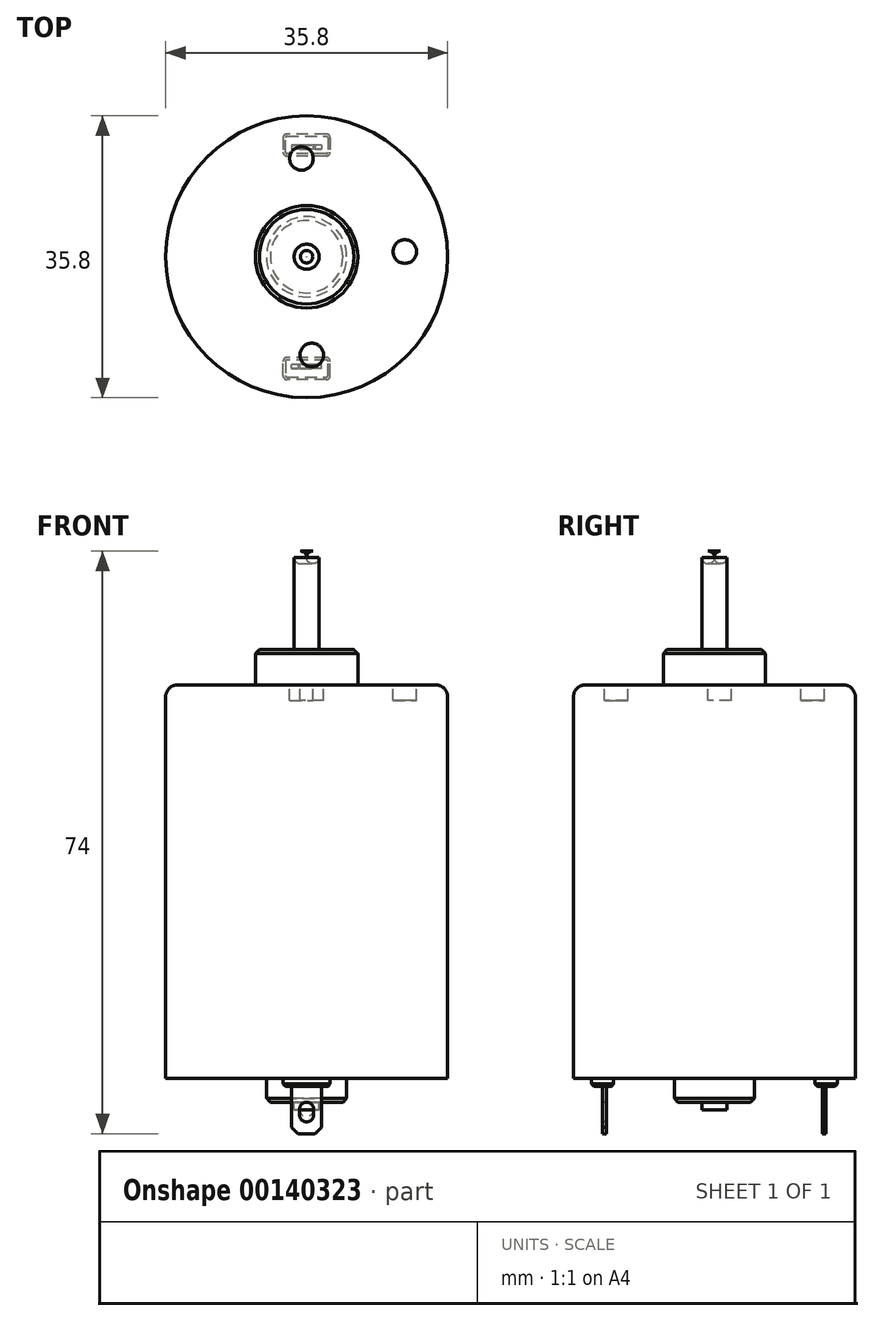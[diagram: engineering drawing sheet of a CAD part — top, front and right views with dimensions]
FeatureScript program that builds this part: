
annotation { "Feature Type Name" : "Feature", "Feature Type Description" : "" }
export const myFeature = defineFeature(function(context is Context, id is Id, definition is map)
    precondition{}
    {
        {
            var Q0;
            Q0=qCreatedBy(makeId("Top.planeOp"),FACE);
            var sketch = newSketch(context, id + "F0", { "sketchPlane" : qUnion([Q0])});
            skCircle(sketch, "E0", {"center": v(0, 0) * mm, "radius": 17.9 * mm});
            skSolve(sketch);
        }
        {
            var Q0;
            Q0=makeQuery(id+"F0.imprint","IMPRINT",FACE,{"disambiguationData":[TD([[makeQuery(id+"F0.imprint","IMPRINT",EDGE,{"derivedFrom":sQuery(id+"F0.wireOp",EDGE,"E0")}),1.0]])]});
            extrude(context, id + "F1", {"entities" : qUnion([Q0]), "depth" : 50 * mm});
        }
        {
            var Q0;
            Q0=makeQuery(id+"F1.opExtrude","CAP_FACE",FACE,{"disambiguationData":[OSD([sQuery(id+"F0.wireOp",EDGE,"E0")])],"isStart":true});
            var sketch = newSketch(context, id + "F2", { "sketchPlane" : qUnion([Q0])});
            skCircle(sketch, "E1", {"center": v(0, 0) * mm, "radius": 5.1 * mm});
            skSolve(sketch);
        }
        {
            var Q0;
            Q0=makeQuery(id+"F2.imprint","IMPRINT",FACE,{"disambiguationData":[TD([[makeQuery(id+"F2.imprint","IMPRINT",EDGE,{"derivedFrom":sQuery(id+"F2.wireOp",EDGE,"E1")}),1.0]])]});
            extrude(context, id + "F3", {"entities" : qUnion([Q0]), "operationType" : NewBodyOperationType.ADD, "depth" : 3 * mm});
        }
        {
            var Q0;
            Q0=makeQuery(id+"F3.opExtrude","CAP_FACE",FACE,{"disambiguationData":[OSD([sQuery(id+"F2.wireOp",EDGE,"E1")])],"isStart":false});
            var sketch = newSketch(context, id + "F4", { "sketchPlane" : qUnion([Q0])});
            skCircle(sketch, "E2", {"center": v(0, 0) * mm, "radius": 1.58 * mm});
            skSolve(sketch);
        }
        {
            var Q0;
            Q0=makeQuery(id+"F4.imprint","IMPRINT",FACE,{"disambiguationData":[TD([[makeQuery(id+"F4.imprint","IMPRINT",EDGE,{"derivedFrom":sQuery(id+"F4.wireOp",EDGE,"E2")}),1.0]])]});
            extrude(context, id + "F5", {"entities" : qUnion([Q0]), "operationType" : NewBodyOperationType.ADD, "depth" : 1 * mm});
        }
        {
            var Q0;
            Q0=makeQuery(id+"F1.opExtrude","CAP_FACE",FACE,{"disambiguationData":[OSD([sQuery(id+"F0.wireOp",EDGE,"E0")])],"isStart":false});
            var sketch = newSketch(context, id + "F6", { "sketchPlane" : qUnion([Q0])});
            skCircle(sketch, "E3", {"center": v(0, 0) * mm, "radius": 6.5 * mm});
            skSolve(sketch);
        }
        {
            var Q0;
            Q0=makeQuery(id+"F6.imprint","IMPRINT",FACE,{"disambiguationData":[TD([[makeQuery(id+"F6.imprint","IMPRINT",EDGE,{"derivedFrom":sQuery(id+"F6.wireOp",EDGE,"E3")}),1.0]])]});
            extrude(context, id + "F7", {"entities" : qUnion([Q0]), "operationType" : NewBodyOperationType.ADD, "depth" : 4.5 * mm});
        }
        {
            var Q0;
            Q0=makeQuery(id+"F5.opExtrude","CAP_FACE",FACE,{"disambiguationData":[OSD([sQuery(id+"F4.wireOp",EDGE,"E2")])],"isStart":false});
            extrude(context, id + "F8", {"entities" : qUnion([Q0]), "operationType" : NewBodyOperationType.ADD, "oppositeDirection" : true, "depth" : 71 * mm});
        }
        {
            var Q0;
            Q0=makeQuery(id+"F1.opExtrude","CAP_FACE",FACE,{"disambiguationData":[OSD([sQuery(id+"F0.wireOp",EDGE,"E0")])],"isStart":true});
            var sketch = newSketch(context, id + "F9", { "sketchPlane" : qUnion([Q0])});
            skLineSegment(sketch, "E4.bottom", {"start": v(3, -15.6) * mm, "end": v(-3, -15.6) * mm});
            skLineSegment(sketch, "E4.top", {"start": v(3, -12.8) * mm, "end": v(-3, -12.8) * mm});
            skLineSegment(sketch, "E4.left", {"start": v(3, -15.6) * mm, "end": v(3, -12.8) * mm});
            skLineSegment(sketch, "E4.right", {"start": v(-3, -15.6) * mm, "end": v(-3, -12.8) * mm});
            skLineSegment(sketch, "E5", {"start": v(0, 0) * mm, "end": v(0, -12.8) * mm, "construction": true});
            skSolve(sketch);
        }
        {
            var Q0;
            Q0=makeQuery(id+"F9.imprint","IMPRINT",FACE,{"disambiguationData":[TD([[makeQuery(id+"F9.imprint","IMPRINT",EDGE,{"derivedFrom":sQuery(id+"F9.wireOp",EDGE,"E4.bottom")}),-1.0]])]});
            extrude(context, id + "F10", {"entities" : qUnion([Q0]), "depth" : 1 * mm});
        }
        {
            var Q0;
            Q0=makeQuery(id+"F10.opExtrude","CAP_FACE",FACE,{"disambiguationData":[OSD([sQuery(id+"F9.wireOp",EDGE,"E4.bottom"),sQuery(id+"F9.wireOp",EDGE,"E4.top"),sQuery(id+"F9.wireOp",EDGE,"E4.left"),sQuery(id+"F9.wireOp",EDGE,"E4.right")])],"isStart":false});
            var sketch = newSketch(context, id + "F11", { "sketchPlane" : qUnion([Q0])});
            skLineSegment(sketch, "E6.bottom", {"start": v(1.9, -14.2) * mm, "end": v(-1.9, -14.2) * mm});
            skLineSegment(sketch, "E6.top", {"start": v(1.9, -13.7) * mm, "end": v(-1.9, -13.7) * mm});
            skLineSegment(sketch, "E6.left", {"start": v(1.9, -14.2) * mm, "end": v(1.9, -13.7) * mm});
            skLineSegment(sketch, "E6.right", {"start": v(-1.9, -14.2) * mm, "end": v(-1.9, -13.7) * mm});
            skLineSegment(sketch, "E7", {"start": v(0, -12.8) * mm, "end": v(0, -13.7) * mm, "construction": true});
            skSolve(sketch);
        }
        {
            var Q0;
            Q0=makeQuery(id+"F11.imprint","IMPRINT",FACE,{"disambiguationData":[TD([[makeQuery(id+"F11.imprint","IMPRINT",EDGE,{"derivedFrom":sQuery(id+"F11.wireOp",EDGE,"E6.bottom")}),-1.0]])]});
            extrude(context, id + "F12", {"entities" : qUnion([Q0]), "operationType" : NewBodyOperationType.ADD, "depth" : 6 * mm});
        }
        {
            var Q0;
            Q0=makeQuery(id+"F12.opExtrude","CAP_EDGE",EDGE,{"disambiguationData":[OSD([sQuery(id+"F11.wireOp",EDGE,"E6.left")])],"isStart":false});
            var Q1;
            Q1=makeQuery(id+"F12.opExtrude","CAP_EDGE",EDGE,{"disambiguationData":[OSD([sQuery(id+"F11.wireOp",EDGE,"E6.right")])],"isStart":false});
            chamfer(context, id + "F13", {"entities" : qUnion([Q0, Q1]), "width" : .8 * mm, "tangentPropagation" : true});
        }
        {
            var Q0;
            Q0=makeQuery(id+"F10.opExtrude","SWEPT_EDGE",EDGE,{"disambiguationData":[OSD([sQuery(id+"F9.wireOp",EDGE,"E4.bottom"),sQuery(id+"F9.wireOp",EDGE,"E4.left")])]});
            var Q1;
            Q1=makeQuery(id+"F10.opExtrude","SWEPT_EDGE",EDGE,{"disambiguationData":[OSD([sQuery(id+"F9.wireOp",EDGE,"E4.bottom"),sQuery(id+"F9.wireOp",EDGE,"E4.right")])]});
            var Q2;
            Q2=makeQuery(id+"F10.opExtrude","SWEPT_EDGE",EDGE,{"disambiguationData":[OSD([sQuery(id+"F9.wireOp",EDGE,"E4.top"),sQuery(id+"F9.wireOp",EDGE,"E4.left")])]});
            var Q3;
            Q3=makeQuery(id+"F10.opExtrude","SWEPT_EDGE",EDGE,{"disambiguationData":[OSD([sQuery(id+"F9.wireOp",EDGE,"E4.top"),sQuery(id+"F9.wireOp",EDGE,"E4.right")])]});
            fillet(context, id + "F14", {"entities" : qUnion([Q0, Q1, Q2, Q3]), "radius" : .5 * mm, "tangentPropagation" : true, "allowEdgeOverflow" : false});
        }
        {
            var Q0;
            Q0=makeQuery(id+"F10.opExtrude","CAP_EDGE",EDGE,{"disambiguationData":[OSD([sQuery(id+"F9.wireOp",EDGE,"E4.top")])],"isStart":false});
            chamfer(context, id + "F15", {"entities" : qUnion([Q0]), "width" : .3 * mm, "tangentPropagation" : true});
        }
        {
            var Q0;
            Q0=makeQuery(id+"F12.opExtrude","SWEPT_FACE",FACE,{"disambiguationData":[OSD([sQuery(id+"F11.wireOp",EDGE,"E6.bottom")])]});
            var sketch = newSketch(context, id + "F16", { "sketchPlane" : qUnion([Q0])});
            skLineSegment(sketch, "E8", {"start": v(0.9, -3.9) * mm, "end": v(0.9, -4.6) * mm});
            skLineSegment(sketch, "E9", {"start": v(-0.9, -4.6) * mm, "end": v(-0.9, -3.9) * mm});
            skArc(sketch, "E10", {"start": v(0.9, -3.9) * mm, "mid": v(0, -3) * mm, "end": v(-0.9, -3.9) * mm});
            skArc(sketch, "E11", {"start": v(0.9, -4.6) * mm, "mid": v(0, -5.5) * mm, "end": v(-0.9, -4.6) * mm});
            skLineSegment(sketch, "E12", {"start": v(0, -7) * mm, "end": v(0, -5.5) * mm, "construction": true});
            skLineSegment(sketch, "E13", {"start": v(0, -3) * mm, "end": v(0, -5.5) * mm, "construction": true});
            skSolve(sketch);
        }
        {
            var Q0;
            Q0=makeQuery(id+"F16.imprint","IMPRINT",FACE,{"disambiguationData":[TD([[makeQuery(id+"F16.imprint","IMPRINT",EDGE,{"derivedFrom":sQuery(id+"F16.wireOp",EDGE,"E8")}),-1.0]])]});
            extrude(context, id + "F17", {"entities" : qUnion([Q0]), "operationType" : NewBodyOperationType.REMOVE, "oppositeDirection" : true, "depth" : 1 * mm});
        }
        {
            var Q0;
            Q0=makeQuery(id+"F10.opExtrude","SWEPT_BODY",BODY,{"disambiguationData":[OSD([sQuery(id+"F9.wireOp",EDGE,"E4.bottom"),sQuery(id+"F9.wireOp",EDGE,"E4.top"),sQuery(id+"F9.wireOp",EDGE,"E4.left"),sQuery(id+"F9.wireOp",EDGE,"E4.right")])]});
            var Q1;
            Q1=qCreatedBy(makeId("Front.planeOp"),FACE);
            mirror(context, id + "F18", {"operationType" : NewBodyOperationType.ADD, "entities" : qUnion([Q0]), "mirrorPlane" : qUnion([Q1])});
        }
        {
            var Q0;
            Q0=makeQuery(id+"F3.opExtrude","CAP_EDGE",EDGE,{"disambiguationData":[OSD([sQuery(id+"F2.wireOp",EDGE,"E1")])],"isStart":false});
            chamfer(context, id + "F19", {"entities" : qUnion([Q0]), "width" : .5 * mm, "tangentPropagation" : true});
        }
        {
            var Q0;
            Q0=makeQuery(id+"F7.opExtrude","CAP_EDGE",EDGE,{"disambiguationData":[OSD([sQuery(id+"F6.wireOp",EDGE,"E3")])],"isStart":false});
            chamfer(context, id + "F20", {"entities" : qUnion([Q0]), "width" : .5 * mm, "tangentPropagation" : true});
        }
        {
            var Q0;
            Q0=makeQuery(id+"F1.opExtrude","CAP_EDGE",EDGE,{"disambiguationData":[OSD([sQuery(id+"F0.wireOp",EDGE,"E0")])],"isStart":false});
            fillet(context, id + "F21", {"entities" : qUnion([Q0]), "radius" : 1.5 * mm, "tangentPropagation" : true, "allowEdgeOverflow" : false});
        }
        {
            var Q0;
            Q0=makeQuery(id+"F8.opExtrude","CAP_EDGE",EDGE,{"disambiguationData":[OSD([sQuery(id+"F4.wireOp",EDGE,"E2")])],"isStart":false});
            fillet(context, id + "F22", {"entities" : qUnion([Q0]), "radius" : .8 * mm, "tangentPropagation" : true, "allowEdgeOverflow" : false});
        }
        {
            var Q0;
            Q0=makeQuery(id+"F1.opExtrude","CAP_FACE",FACE,{"disambiguationData":[OSD([sQuery(id+"F0.wireOp",EDGE,"E0")])],"isStart":false});
            var sketch = newSketch(context, id + "F23", { "sketchPlane" : qUnion([Q0])});
            skCircle(sketch, "E14", {"center": v(0.65, -12.48) * mm, "radius": 1.5 * mm});
            skLineSegment(sketch, "E15", {"start": v(0.65, -12.48) * mm, "end": v(0, 0) * mm, "construction": true});
            skLineSegment(sketch, "E16", {"start": v(0, 0) * mm, "end": v(0, 20.99) * mm, "construction": true});
            skSolve(sketch);
        }
        {
            var Q0;
            Q0=makeQuery(id+"F23.imprint","IMPRINT",FACE,{"disambiguationData":[TD([[makeQuery(id+"F23.imprint","IMPRINT",EDGE,{"derivedFrom":sQuery(id+"F23.wireOp",EDGE,"E14")}),1.0]])]});
            extrude(context, id + "F24", {"entities" : qUnion([Q0]), "oppositeDirection" : true, "depth" : 2 * mm});
        }
        {
            var Q0;
            Q0=makeQuery(id+"F24.opExtrude","SWEPT_BODY",BODY,{"disambiguationData":[OSD([sQuery(id+"F23.wireOp",EDGE,"E14")])]});
            var Q1;
            Q1=makeQuery(id+"F8.opExtrude","SWEPT_FACE",FACE,{"disambiguationData":[OSD([sQuery(id+"F4.wireOp",EDGE,"E2")])]});
            circularPattern(context, id + "F25", {"operationType" : NewBodyOperationType.REMOVE, "entities" : qUnion([Q0]), "axis" : qUnion([Q1]), "angle" : 90 * degree, "instanceCount" : 3, "oppositeDirection" : true});
        }
    });
